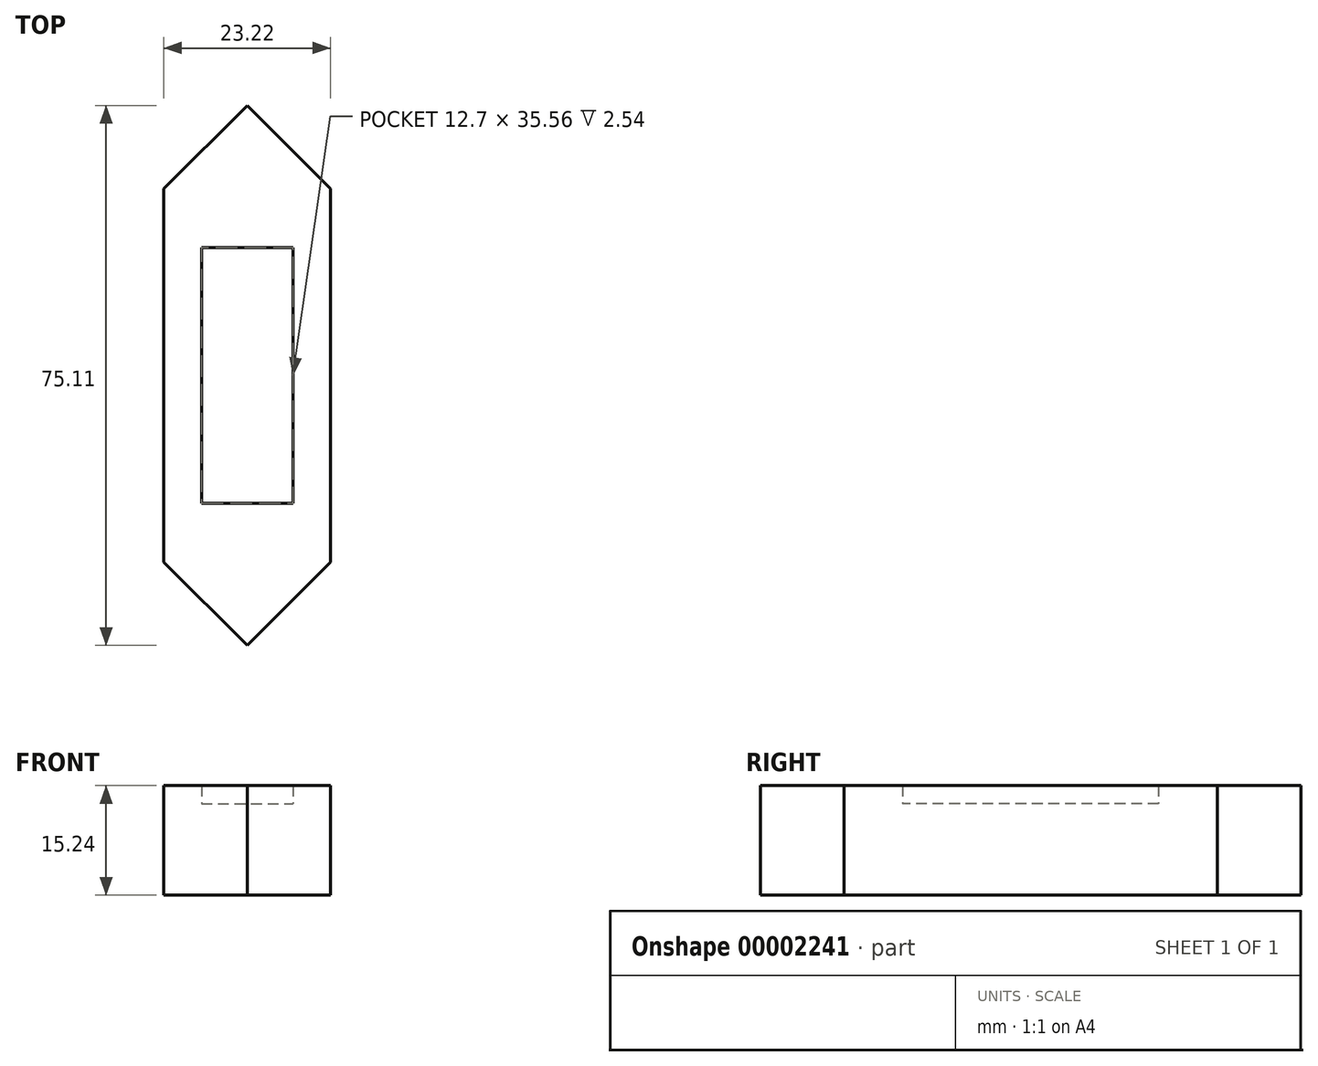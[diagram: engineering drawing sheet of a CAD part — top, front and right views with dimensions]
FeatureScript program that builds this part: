
annotation { "Feature Type Name" : "Feature", "Feature Type Description" : "" }
export const myFeature = defineFeature(function(context is Context, id is Id, definition is map)
    precondition{}
    {
        {
            var Q0;
            Q0=qCreatedBy(makeId("Top.planeOp"),FACE);
            var sketch = newSketch(context, id + "F0", { "sketchPlane" : qUnion([Q0])});
            skLineSegment(sketch, "E0", {"start": v(1.31, 50.3) * mm, "end": v(-16.65, 32.33) * mm, "construction": true});
            skLineSegment(sketch, "E1", {"start": v(-16.65, 32.33) * mm, "end": v(-16.65, -24.82) * mm, "construction": true});
            skLineSegment(sketch, "E2", {"start": v(-16.65, -24.82) * mm, "end": v(1.31, -42.78) * mm, "construction": true});
            skLineSegment(sketch, "E3", {"start": v(1.31, -42.78) * mm, "end": v(19.27, -24.82) * mm, "construction": true});
            skLineSegment(sketch, "E4", {"start": v(19.27, -24.82) * mm, "end": v(19.27, 32.33) * mm, "construction": true});
            skLineSegment(sketch, "E5", {"start": v(19.27, 32.33) * mm, "end": v(1.31, 50.3) * mm, "construction": true});
            skLineSegment(sketch, "E6.0", {"start": v(1.31, 41.31) * mm, "end": v(-10.3, 29.7) * mm});
            skLineSegment(sketch, "E6.1", {"start": v(12.92, 29.7) * mm, "end": v(1.31, 41.31) * mm});
            skLineSegment(sketch, "E6.2", {"start": v(12.92, -22.19) * mm, "end": v(12.92, 29.7) * mm});
            skLineSegment(sketch, "E6.3", {"start": v(1.31, -33.8) * mm, "end": v(12.92, -22.19) * mm});
            skLineSegment(sketch, "E6.4", {"start": v(-10.3, -22.19) * mm, "end": v(1.31, -33.8) * mm});
            skLineSegment(sketch, "E6.5", {"start": v(-10.3, 29.7) * mm, "end": v(-10.3, -22.19) * mm});
            skLineSegment(sketch, "E7.bottom", {"start": v(-5.04, 21.54) * mm, "end": v(7.66, 21.54) * mm});
            skLineSegment(sketch, "E7.top", {"start": v(-5.04, -14.02) * mm, "end": v(7.66, -14.02) * mm});
            skLineSegment(sketch, "E7.left", {"start": v(-5.04, 21.54) * mm, "end": v(-5.04, -14.02) * mm});
            skLineSegment(sketch, "E7.right", {"start": v(7.66, 21.54) * mm, "end": v(7.66, -14.02) * mm});
            skLineSegment(sketch, "E8", {"start": v(-10.3, 29.7) * mm, "end": v(-5.04, 21.54) * mm, "construction": true});
            skLineSegment(sketch, "E9", {"start": v(12.92, 29.7) * mm, "end": v(7.66, 21.54) * mm, "construction": true});
            skLineSegment(sketch, "E10", {"start": v(12.92, -22.19) * mm, "end": v(7.66, -14.02) * mm, "construction": true});
            skLineSegment(sketch, "E11", {"start": v(-10.3, -22.19) * mm, "end": v(-5.04, -14.02) * mm, "construction": true});
            skSolve(sketch);
        }
        {
            var Q0;
            Q0=makeQuery(id+"F0.imprint","IMPRINT",FACE,{"disambiguationData":[TD([[makeQuery(id+"F0.imprint","IMPRINT",EDGE,{"derivedFrom":sQuery(id+"F0.wireOp",EDGE,"E6.0")}),1.0]])]});
            extrude(context, id + "F1", {"entities" : qUnion([Q0]), "depth" : 15.24 * mm});
        }
        {
            var Q0;
            Q0=makeQuery(id+"F0.imprint","IMPRINT",FACE,{"disambiguationData":[TD([[makeQuery(id+"F0.imprint","IMPRINT",EDGE,{"derivedFrom":sQuery(id+"F0.wireOp",EDGE,"E7.bottom")}),-1.0]])]});
            extrude(context, id + "F2", {"entities" : qUnion([Q0]), "operationType" : NewBodyOperationType.ADD, "depth" : 12.7 * mm});
        }
    });
